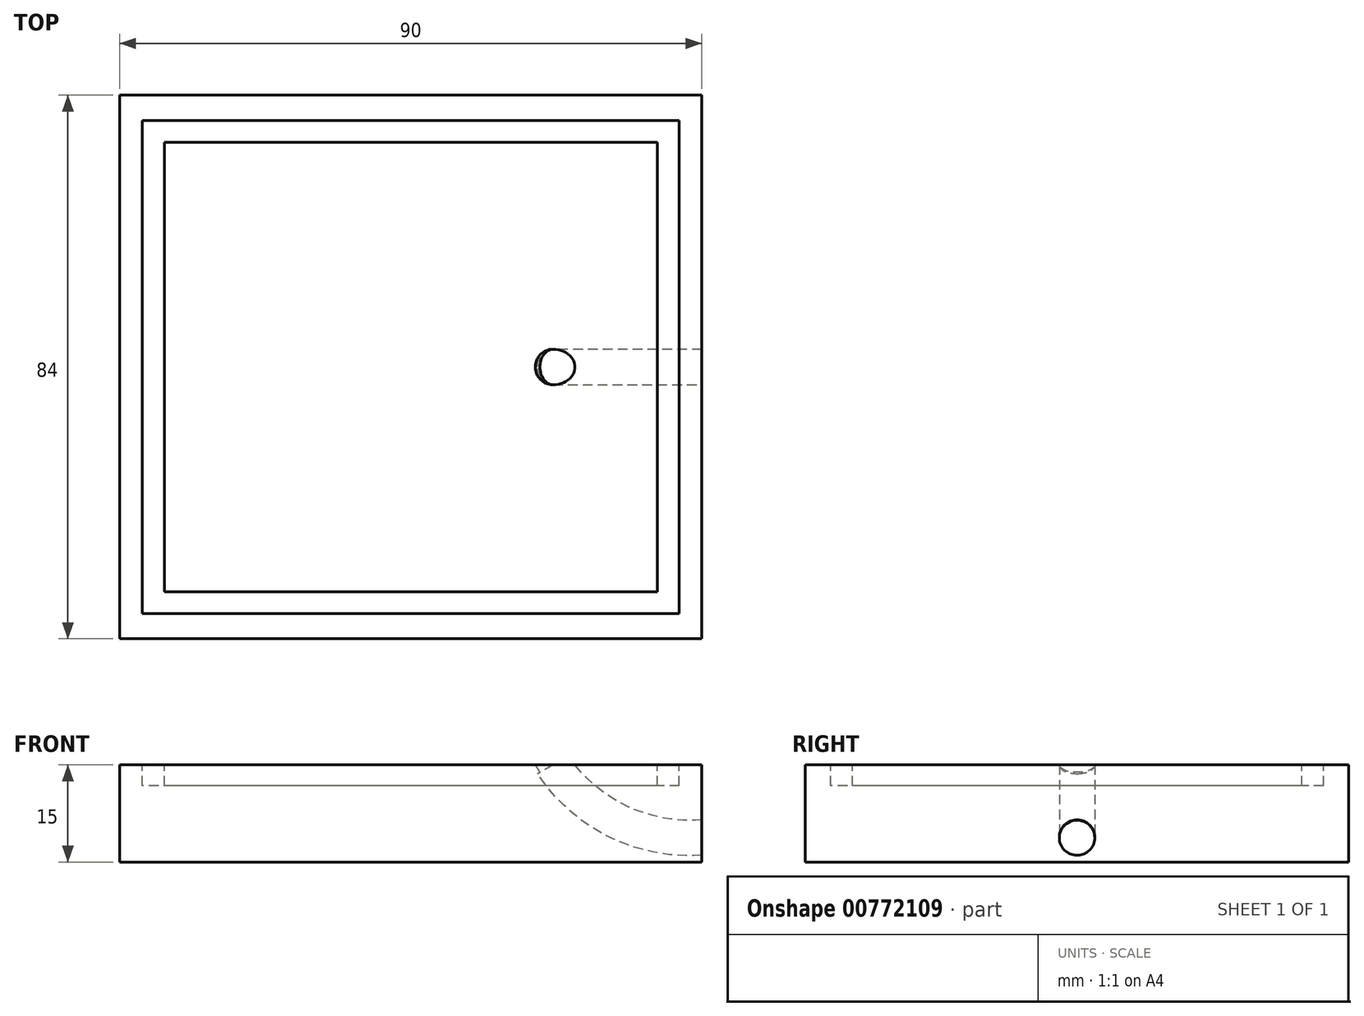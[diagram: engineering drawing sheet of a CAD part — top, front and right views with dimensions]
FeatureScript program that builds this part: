
annotation { "Feature Type Name" : "Feature", "Feature Type Description" : "" }
export const myFeature = defineFeature(function(context is Context, id is Id, definition is map)
    precondition{}
    {
        {
            var Q0;
            Q0=qCreatedBy(makeId("Top.planeOp"),FACE);
            var sketch = newSketch(context, id + "F0", { "sketchPlane" : qUnion([Q0])});
            skLineSegment(sketch, "E0.bottom", {"start": v(45, 42) * mm, "end": v(-45, 42) * mm});
            skLineSegment(sketch, "E0.top", {"start": v(45, -42) * mm, "end": v(-45, -42) * mm});
            skLineSegment(sketch, "E0.left", {"start": v(45, 42) * mm, "end": v(45, -42) * mm});
            skLineSegment(sketch, "E0.right", {"start": v(-45, 42) * mm, "end": v(-45, -42) * mm});
            skPoint(sketch, "E0.middle", {"position": v(0, 0) * mm});
            skSolve(sketch);
        }
        {
            var Q0;
            Q0 = qSketchRegion(id + "F0", true);
            extrude(context, id + "F1", {"entities" : qUnion([Q0]), "depth" : 15 * mm, "offsetDistance" : 25 * mm});
        }
        {
            var Q0;
            Q0=makeQuery(id+"F1.opExtrude","CAP_FACE",FACE,{"disambiguationData":[OSD([sQuery(id+"F0.wireOp",EDGE,"E0.bottom"),sQuery(id+"F0.wireOp",EDGE,"E0.top"),sQuery(id+"F0.wireOp",EDGE,"E0.left"),sQuery(id+"F0.wireOp",EDGE,"E0.right")])],"isStart":false});
            var sketch = newSketch(context, id + "F2", { "sketchPlane" : qUnion([Q0])});
            skLineSegment(sketch, "E1.bottom", {"start": v(41.5, 38.1) * mm, "end": v(-41.5, 38.1) * mm});
            skLineSegment(sketch, "E1.top", {"start": v(41.5, -38.1) * mm, "end": v(-41.5, -38.1) * mm});
            skLineSegment(sketch, "E1.left", {"start": v(41.5, 38.1) * mm, "end": v(41.5, -38.1) * mm});
            skLineSegment(sketch, "E1.right", {"start": v(-41.5, 38.1) * mm, "end": v(-41.5, -38.1) * mm});
            skPoint(sketch, "E1.middle", {"position": v(0, 0) * mm});
            skLineSegment(sketch, "E2.bottom", {"start": v(38.1, 34.75) * mm, "end": v(-38.1, 34.75) * mm});
            skLineSegment(sketch, "E2.top", {"start": v(38.1, -34.75) * mm, "end": v(-38.1, -34.75) * mm});
            skLineSegment(sketch, "E2.left", {"start": v(38.1, 34.75) * mm, "end": v(38.1, -34.75) * mm});
            skLineSegment(sketch, "E2.right", {"start": v(-38.1, 34.75) * mm, "end": v(-38.1, -34.75) * mm});
            skSolve(sketch);
        }
        {
            var Q0;
            Q0 = qSketchRegion(id + "F2", true);
            extrude(context, id + "F3", {"entities" : qUnion([Q0]), "operationType" : NewBodyOperationType.REMOVE, "oppositeDirection" : true, "depth" : 3.2 * mm, "offsetDistance" : 25 * mm});
        }
        {
            var Q0;
            Q0=makeQuery(id+"F3.boolean.opBoolean","SPLIT",FACE,{"disambiguationData":[TD([makeQuery(id+"F3.opExtrude","SWEPT_FACE",FACE,{"disambiguationData":[OSD([sQuery(id+"F2.wireOp",EDGE,"E2.bottom")])]})])],"derivedFrom":makeQuery(id+"F1.opExtrude","CAP_FACE",FACE,{"disambiguationData":[OSD([sQuery(id+"F0.wireOp",EDGE,"E0.bottom"),sQuery(id+"F0.wireOp",EDGE,"E0.top"),sQuery(id+"F0.wireOp",EDGE,"E0.left"),sQuery(id+"F0.wireOp",EDGE,"E0.right")])],"isStart":false})});
            var sketch = newSketch(context, id + "F4", { "sketchPlane" : qUnion([Q0])});
            skCircle(sketch, "E3", {"center": v(22, 0) * mm, "radius": 2.75 * mm});
            skSolve(sketch);
        }
        {
            var Q0;
            Q0=makeQuery(id+"F1.opExtrude","SWEPT_FACE",FACE,{"disambiguationData":[OSD([sQuery(id+"F0.wireOp",EDGE,"E0.left")])]});
            var sketch = newSketch(context, id + "F5", { "sketchPlane" : qUnion([Q0])});
            skCircle(sketch, "E4", {"center": v(0, 3.78) * mm, "radius": 2.75 * mm});
            skSolve(sketch);
        }
        {
            var Q0;
            Q0=qCreatedBy(makeId("Front.planeOp"),FACE);
            var sketch = newSketch(context, id + "F6", { "sketchPlane" : qUnion([Q0])});
            skArc(sketch, "E5", {"start": v(22, 15) * mm, "mid": v(31.98, 6.28) * mm, "end": v(45, 3.78) * mm});
            skSolve(sketch);
        }
        {
            var Q0;
            Q0=makeQuery(id+"F4.imprint","IMPRINT",FACE,{"disambiguationData":[TD([[makeQuery(id+"F4.imprint","IMPRINT",EDGE,{"derivedFrom":sQuery(id+"F4.wireOp",EDGE,"E3")}),1.0]])]});
            var Q1;
            Q1=makeQuery(id+"F5.imprint","IMPRINT",FACE,{"disambiguationData":[TD([[makeQuery(id+"F5.imprint","IMPRINT",EDGE,{"derivedFrom":sQuery(id+"F5.wireOp",EDGE,"E4")}),1.0]])]});
            var Q2;
            Q2=sQuery(id+"F6.wireOp",EDGE,"E5");
            sweep(context, id + "F7", {"operationType" : NewBodyOperationType.REMOVE, "profiles" : qUnion([Q0, Q1]), "path" : qUnion([Q2])});
        }
    });
